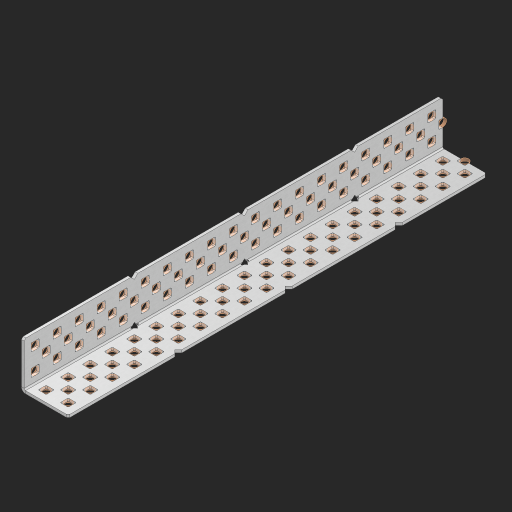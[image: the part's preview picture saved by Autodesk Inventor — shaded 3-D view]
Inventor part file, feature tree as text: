
AUTODESK INVENTOR PART (.ipt)
format: ipt  version: 2023 (Build 270158000, 158)  size: 1,482,752 bytes
history: native  units: in
note: dims shown in document units (in); Inventor stores cm internally (conversion verified against a paired STEP export)
features: other x120, extrude x112, sheet_metal_op x8, sketch x7, pattern_linear x2, mirror x1, chamfer x1
ambient origin geometry x8: Origin, YZ Plane, XZ Plane, XY Plane, X Axis, Y Axis, Z Axis, Center Point
bodies: Solid1 (feature_tree), Body (feature_tree)
feature tree (251):
  sheet_metal_op  "Flanges"
  sheet_metal_op  "Body Pattern"
  pattern_linear  "Center Pattern"  Spacing1=1.0in  [1 undecoded]
  other  "Arc Length"
  pattern_linear  "Notch Pattern"  Spacing1=0.25in  [1 undecoded]
  other  "Diagonal Plane"
  mirror  "Everything Mirrored"
  chamfer  "End Chamfer"
  sketch  "Sketch1"  dims[d0=1.0in]
  other  "Plate1"
  sketch  "Sketch2"  dims[d1=9.5in]
  other  "Plate2"
  sheet_metal_op  "Bend1"
  sheet_metal_op  "Corner1"
  sketch  "Sketch8"  dims[d2=0.0625in]
  sketch  "Sketch9"  dims[d3=0.0625in]
  other  "Srf91"
  sheet_metal_op  "Body Pattern Sketch"
  other  "Srf92"
  sketch  "Sketch13"  dims[d4=0.0312in]
  sketch  "Sketch15"  dims[d5=0.125in]
  sketch  "Sketch16"  dims[d6=0.0625in d7=1.0in d8=90.0deg d9=0.0312in d10=0.25in d11=0.0625in d12=0.0625in d49=0.182in d50=0.02in d52=0.25in d53=0.0625in d54=0.0in d55=0.172in d56=1.0in d57=0.0in d60=7.4803in d62=0.5in d63=0.7874in d65=0.5in d85=0.1473in d86=0.1782in d89=0.0625in d90=0.0in d91=0.04in d92=0.0491in d95=2.5in d96=0.04in d97=0.25in d98=45.0deg d99=0.25in d106=0.182in d107=0.02in d108=0.5in d110=0.0625in d111=0.0in d112=0.172in d113=0.5in d114=0.0in d117=0.5in d123=0.25in d125=0.25in d126=0.0491in d127=0.1473in d128=0.08in d129=0.04in d130=2.5in]
  other  "Srf786"
  other  "Srf856"
  other  "Srf857"
  other  "Srf858"
  other  "Srf859"
  other  "Srf860"
  other  "Srf861"
  other  "Srf889"
  other  "Srf890"
  other  "Srf891"
  other  "Srf1275"
  other  "Srf1276"
  other  "Srf1278"
  other  "Srf1279"
  other  "Srf1280"
  other  "Srf1281"
  other  "Srf1282"
  other  "Srf1283"
  other  "Srf1277"
  other  "Srf1285"
  other  "Srf1286"
  other  "Srf1287"
  other  "Srf1383"
  other  "Srf1384"
  other  "Srf1385"
  other  "Srf1386"
  other  "Srf1387"
  other  "Srf1388"
  other  "Srf1389"
  other  "Srf1390"
  other  "Srf1391"
  other  "Srf1392"
  other  "Srf1393"
  other  "Srf1394"
  other  "Srf1395"
  other  "Srf1396"
  other  "Srf1397"
  other  "Srf1398"
  other  "Srf1399"
  other  "Srf1400"
  other  "Srf1401"
  other  "Srf1402"
  other  "Srf1403"
  other  "Srf1404"
  other  "Srf1405"
  other  "Srf1406"
  other  "Srf1407"
  other  "Srf1408"
  other  "Srf1409"
  other  "Srf1410"
  other  "Srf1411"
  other  "Srf1412"
  other  "Srf1445"
  other  "Srf1446"
  other  "Srf1447"
  other  "Srf1448"
  other  "Srf1449"
  other  "Srf1450"
  other  "Srf1451"
  other  "Srf1452"
  other  "Srf1453"
  other  "Srf1454"
  other  "Srf1455"
  other  "Srf1456"
  other  "Srf1457"
  other  "Srf1458"
  other  "Srf1459"
  other  "Srf1475"
  other  "Srf1476"
  other  "Srf1477"
  other  "Srf1478"
  other  "Srf1479"
  other  "Srf1480"
  other  "Srf1481"
  other  "Srf1482"
  other  "Srf1483"
  other  "Srf1484"
  other  "Srf1485"
  other  "Srf1486"
  other  "Srf1487"
  other  "Srf1488"
  other  "Srf1489"
  other  "Srf1490"
  other  "Srf1491"
  other  "Srf1492"
  other  "Srf1493"
  other  "Srf1494"
  other  "Srf1495"
  other  "Srf1496"
  other  "Srf1497"
  other  "Srf1498"
  other  "Srf1499"
  other  "Srf1500"
  other  "Srf1501"
  other  "Srf1502"
  other  "Srf1503"
  other  "Srf1504"
  other  "Srf1537"
  other  "Srf1538"
  other  "Srf1539"
  other  "Srf1540"
  other  "Srf1541"
  other  "Srf1542"
  other  "Srf1543"
  other  "Srf1544"
  other  "Srf1545"
  other  "Srf1546"
  other  "Srf1547"
  other  "Srf1548"
  other  "Srf1549"
  other  "Srf1550"
  other  "Srf1551"
  sheet_metal_op  "Body Stamp"
  sheet_metal_op  "Body Circle"
  other  "Center Stamp"
  other  "Center Circle"
  sheet_metal_op  "Notch"
  extrude  "ExtrusionSrf92"  Depth=0.0625in
  extrude  "ExtrusionSrf856"  Depth=0.0625in
  extrude  "ExtrusionSrf857"  Depth=0.182in
  extrude  "ExtrusionSrf858"  Depth=0.02in
  extrude  "ExtrusionSrf859"  Depth=0.25in
  extrude  "ExtrusionSrf860"  Depth=0.0625in
  extrude  "ExtrusionSrf861"  TaperAngle=0.0deg  [1 undecoded]
  extrude  "ExtrusionSrf889"  Depth=2.5in
  extrude  "ExtrusionSrf890"  Depth=1.0in TaperAngle=0.0deg
  extrude  "ExtrusionSrf891"  Depth=2.5in
  extrude  "ExtrusionSrf1275"  Depth=0.5in
  extrude  "ExtrusionSrf1276"  Depth=2.5in
  extrude  "ExtrusionSrf1277"  Depth=2.5in
  extrude  "ExtrusionSrf1278"  Depth=0.0625in
  extrude  "ExtrusionSrf1279"  Depth=2.5in TaperAngle=0.0deg
  extrude  "ExtrusionSrf1280"  Depth=2.5in
  extrude  "ExtrusionSrf1281"  Depth=0.25in TaperAngle=45.0deg
  extrude  "ExtrusionSrf1282"  Depth=0.25in
  extrude  "ExtrusionSrf1345"  Depth=0.182in
  extrude  "ExtrusionSrf1346"  Depth=0.02in
  extrude  "ExtrusionSrf1347"  Depth=0.5in
  extrude  "ExtrusionSrf1348"  Depth=0.0625in
  extrude  "ExtrusionSrf1383"  TaperAngle=0.0deg  [1 undecoded]
  extrude  "ExtrusionSrf1384"  Depth=2.5in
  extrude  "ExtrusionSrf1385"  Depth=0.5in TaperAngle=0.0deg
  extrude  "ExtrusionSrf1386"  Depth=0.5in
  extrude  "ExtrusionSrf1387"  Depth=0.25in
  extrude  "ExtrusionSrf1388"  Depth=0.25in
  extrude  "ExtrusionSrf1389"  Depth=2.5in
  extrude  "ExtrusionSrf1390"  Depth=2.5in
  extrude  "ExtrusionSrf1391"  Depth=2.5in
  extrude  "ExtrusionSrf1392"  Depth=2.5in
  extrude  "ExtrusionSrf1393"  Depth=2.5in
  extrude  "ExtrusionSrf1394"  [1 undecoded]
  extrude  "ExtrusionSrf1395"  [1 undecoded]
  extrude  "ExtrusionSrf1396"  [1 undecoded]
  extrude  "ExtrusionSrf1397"  [1 undecoded]
  extrude  "ExtrusionSrf1398"  [1 undecoded]
  extrude  "ExtrusionSrf1399"  [1 undecoded]
  extrude  "ExtrusionSrf1400"  [1 undecoded]
  extrude  "ExtrusionSrf1401"  [1 undecoded]
  extrude  "ExtrusionSrf1402"  [1 undecoded]
  extrude  "ExtrusionSrf1403"  [1 undecoded]
  extrude  "ExtrusionSrf1404"  [1 undecoded]
  extrude  "ExtrusionSrf1405"  [1 undecoded]
  extrude  "ExtrusionSrf1406"  [1 undecoded]
  extrude  "ExtrusionSrf1407"  [1 undecoded]
  extrude  "ExtrusionSrf1408"  [1 undecoded]
  extrude  "ExtrusionSrf1409"  [1 undecoded]
  extrude  "ExtrusionSrf1410"  [1 undecoded]
  extrude  "ExtrusionSrf1411"  [1 undecoded]
  extrude  "ExtrusionSrf1412"  [1 undecoded]
  extrude  "ExtrusionSrf1445"  [1 undecoded]
  extrude  "ExtrusionSrf1446"  [1 undecoded]
  extrude  "ExtrusionSrf1447"  [1 undecoded]
  extrude  "ExtrusionSrf1448"  [1 undecoded]
  extrude  "ExtrusionSrf1449"  [1 undecoded]
  extrude  "ExtrusionSrf1450"  [1 undecoded]
  extrude  "ExtrusionSrf1451"  [1 undecoded]
  extrude  "ExtrusionSrf1452"  [1 undecoded]
  extrude  "ExtrusionSrf1453"  [1 undecoded]
  extrude  "ExtrusionSrf1454"  [1 undecoded]
  extrude  "ExtrusionSrf1455"  [1 undecoded]
  extrude  "ExtrusionSrf1456"  [1 undecoded]
  extrude  "ExtrusionSrf1457"  [1 undecoded]
  extrude  "ExtrusionSrf1458"  [1 undecoded]
  extrude  "ExtrusionSrf1459"  [1 undecoded]
  extrude  "ExtrusionSrf1475"  [1 undecoded]
  extrude  "ExtrusionSrf1476"  [1 undecoded]
  extrude  "ExtrusionSrf1477"  [1 undecoded]
  extrude  "ExtrusionSrf1478"  [1 undecoded]
  extrude  "ExtrusionSrf1479"  [1 undecoded]
  extrude  "ExtrusionSrf1480"  [1 undecoded]
  extrude  "ExtrusionSrf1481"  [1 undecoded]
  extrude  "ExtrusionSrf1482"  [1 undecoded]
  extrude  "ExtrusionSrf1483"  [1 undecoded]
  extrude  "ExtrusionSrf1484"  [1 undecoded]
  extrude  "ExtrusionSrf1485"  [1 undecoded]
  extrude  "ExtrusionSrf1486"  [1 undecoded]
  extrude  "ExtrusionSrf1487"  [1 undecoded]
  extrude  "ExtrusionSrf1488"  [1 undecoded]
  extrude  "ExtrusionSrf1489"  [1 undecoded]
  extrude  "ExtrusionSrf1490"  [1 undecoded]
  extrude  "ExtrusionSrf1491"  [1 undecoded]
  extrude  "ExtrusionSrf1492"  [1 undecoded]
  extrude  "ExtrusionSrf1493"  [1 undecoded]
  extrude  "ExtrusionSrf1494"  [1 undecoded]
  extrude  "ExtrusionSrf1495"  [1 undecoded]
  extrude  "ExtrusionSrf1496"  [1 undecoded]
  extrude  "ExtrusionSrf1497"  [1 undecoded]
  extrude  "ExtrusionSrf1498"  [1 undecoded]
  extrude  "ExtrusionSrf1499"  [1 undecoded]
  extrude  "ExtrusionSrf1500"  [1 undecoded]
  extrude  "ExtrusionSrf1501"  [1 undecoded]
  extrude  "ExtrusionSrf1502"  [1 undecoded]
  extrude  "ExtrusionSrf1503"  [1 undecoded]
  extrude  "ExtrusionSrf1504"  [1 undecoded]
  extrude  "ExtrusionSrf1537"  [1 undecoded]
  extrude  "ExtrusionSrf1538"  [1 undecoded]
  extrude  "ExtrusionSrf1539"  [1 undecoded]
  extrude  "ExtrusionSrf1540"  [1 undecoded]
  extrude  "ExtrusionSrf1541"  [1 undecoded]
  extrude  "ExtrusionSrf1542"  [1 undecoded]
  extrude  "ExtrusionSrf1543"  [1 undecoded]
  extrude  "ExtrusionSrf1544"  [1 undecoded]
  extrude  "ExtrusionSrf1545"  [1 undecoded]
  extrude  "ExtrusionSrf1546"  [1 undecoded]
  extrude  "ExtrusionSrf1547"  [1 undecoded]
  extrude  "ExtrusionSrf1548"  [1 undecoded]
  extrude  "ExtrusionSrf1549"  [1 undecoded]
  extrude  "ExtrusionSrf1550"  [1 undecoded]
  extrude  "ExtrusionSrf1551"  [1 undecoded]
note: 83 required parameter values undecoded (feature->parameter linkage not recoverable at this tier; creation-order binding heuristic only, values carry confidence <= 0.55)
